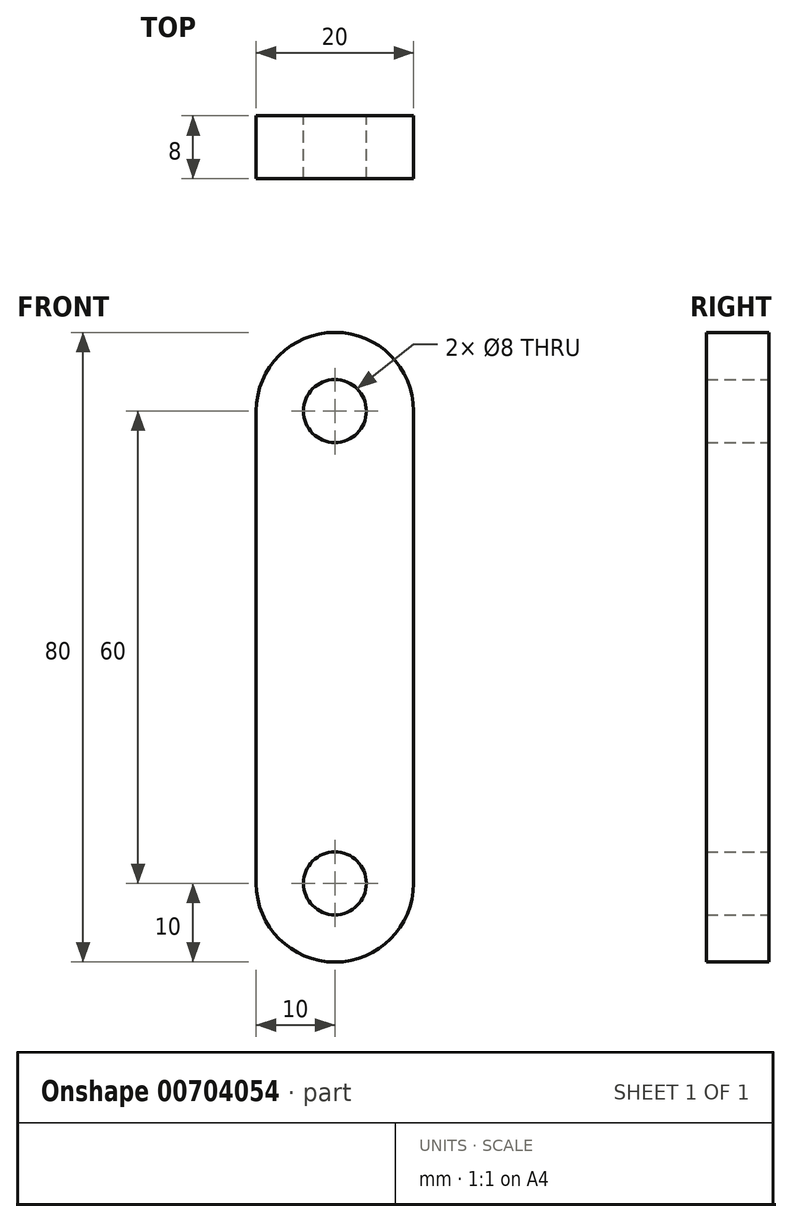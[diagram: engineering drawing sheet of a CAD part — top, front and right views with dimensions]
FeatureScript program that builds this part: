
annotation { "Feature Type Name" : "Feature", "Feature Type Description" : "" }
export const myFeature = defineFeature(function(context is Context, id is Id, definition is map)
    precondition{}
    {
        {
            var Q0;
            Q0=qCreatedBy(makeId("Front.planeOp"),FACE);
            var sketch = newSketch(context, id + "F0", { "sketchPlane" : qUnion([Q0])});
            skCircle(sketch, "E0", {"center": v(0, 0) * mm, "radius": 4 * mm});
            skArc(sketch, "E1", {"start": v(-10, 0) * mm, "mid": v(0, -10) * mm, "end": v(10, 0) * mm});
            skCircle(sketch, "E2", {"center": v(0, 60) * mm, "radius": 4 * mm});
            skLineSegment(sketch, "E3", {"start": v(-10, 60) * mm, "end": v(-10, 0) * mm});
            skLineSegment(sketch, "E4", {"start": v(10, 60) * mm, "end": v(10, 0) * mm});
            skArc(sketch, "E5.trimOffspring", {"start": v(10, 60) * mm, "mid": v(0, 70) * mm, "end": v(-10, 60) * mm});
            skSolve(sketch);
        }
        {
            var Q0;
            Q0=makeQuery(id+"F0.imprint","IMPRINT",FACE,{"disambiguationData":[TD([[makeQuery(id+"F0.imprint","IMPRINT",EDGE,{"derivedFrom":sQuery(id+"F0.wireOp",EDGE,"E0")}),-1.0]])]});
            extrude(context, id + "F1", {"entities" : qUnion([Q0]), "depth" : 8 * mm, "offsetDistance" : 25.4 * mm});
        }
    });
